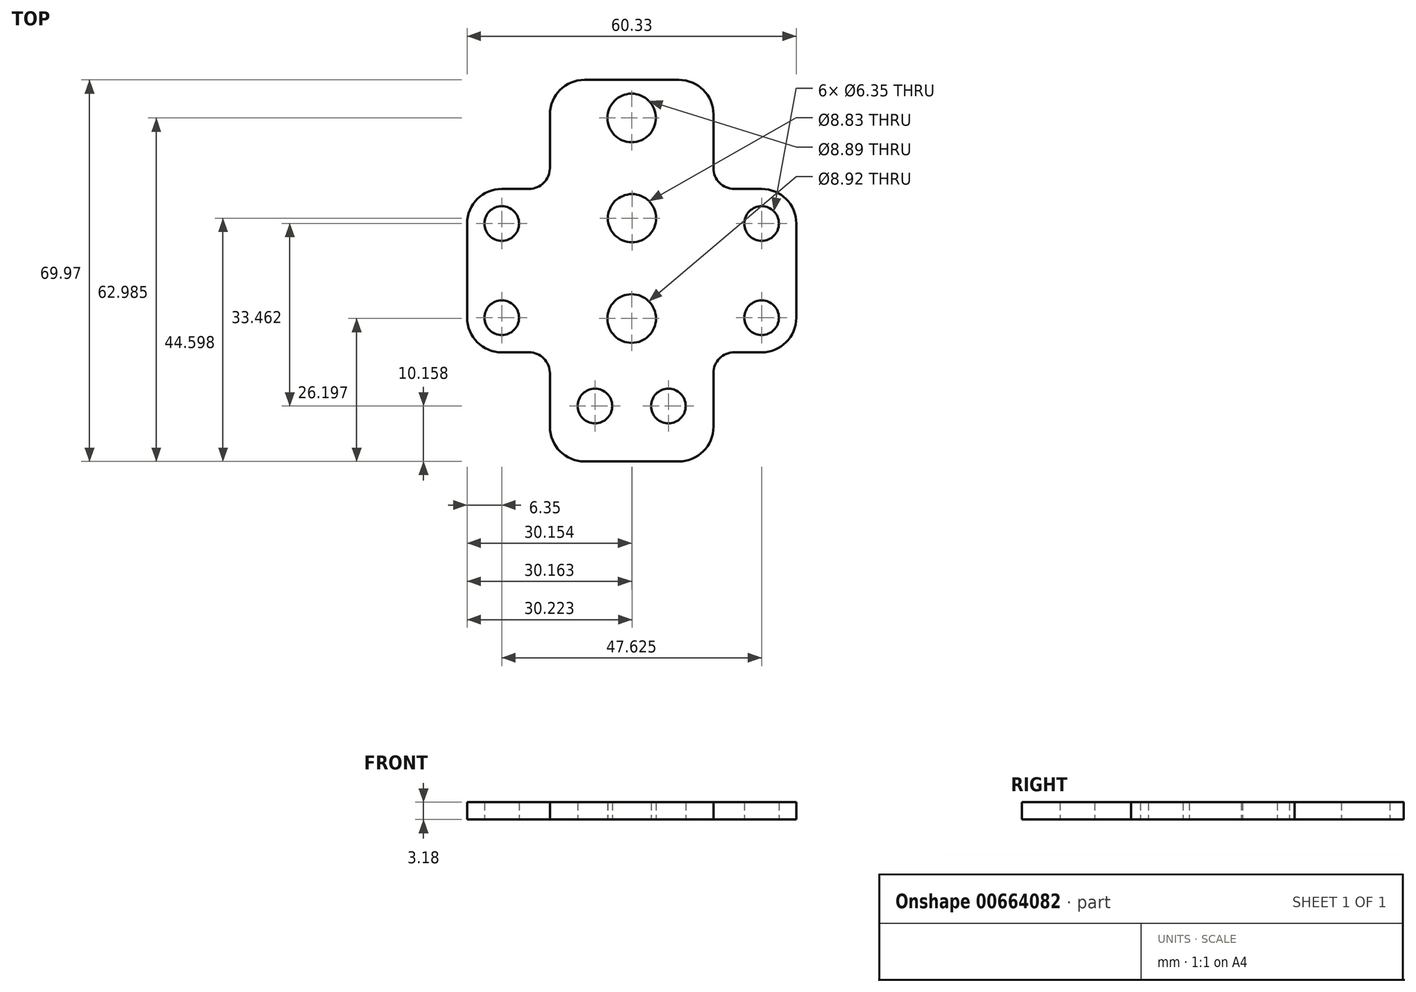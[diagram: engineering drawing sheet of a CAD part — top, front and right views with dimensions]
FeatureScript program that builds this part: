
annotation { "Feature Type Name" : "Feature", "Feature Type Description" : "" }
export const myFeature = defineFeature(function(context is Context, id is Id, definition is map)
    precondition{}
    {
        {
            var Q0;
            Q0=qCreatedBy(makeId("Top.planeOp"),FACE);
            var sketch = newSketch(context, id + "F0", { "sketchPlane" : qUnion([Q0])});
            skLineSegment(sketch, "E0.bottom", {"start": v(6.35, 0) * mm, "end": v(11.36, 0) * mm});
            skLineSegment(sketch, "E0.top", {"start": v(6.35, -29.97) * mm, "end": v(11.36, -29.97) * mm});
            skLineSegment(sketch, "E0.left", {"start": v(0, -6.35) * mm, "end": v(0, -23.62) * mm});
            skLineSegment(sketch, "E0.right", {"start": v(60.32, -6.35) * mm, "end": v(60.32, -23.62) * mm});
            skLineSegment(sketch, "E1.top", {"start": v(21.52, -49.97) * mm, "end": v(38.8, -49.97) * mm});
            skLineSegment(sketch, "E1.left", {"start": v(15.17, -33.78) * mm, "end": v(15.17, -43.62) * mm});
            skLineSegment(sketch, "E1.right", {"start": v(45.15, -33.78) * mm, "end": v(45.15, -43.62) * mm});
            skLineSegment(sketch, "E2.top", {"start": v(21.52, 20) * mm, "end": v(38.8, 20) * mm});
            skLineSegment(sketch, "E2.left", {"start": v(15.17, 3.81) * mm, "end": v(15.17, 13.65) * mm});
            skLineSegment(sketch, "E2.right", {"start": v(45.15, 3.8) * mm, "end": v(45.15, 13.65) * mm});
            skLineSegment(sketch, "E3.trimOffspring", {"start": v(48.96, 0) * mm, "end": v(53.97, 0) * mm});
            skLineSegment(sketch, "E4.trimOffspring", {"start": v(48.96, -29.97) * mm, "end": v(53.97, -29.97) * mm});
            skPoint(sketch, "E5.visualSharp", {"position": v(15.17, 20) * mm});
            skArc(sketch, "E5.filletArc", {"start": v(21.52, 20) * mm, "mid": v(17.03, 18.14) * mm, "end": v(15.17, 13.65) * mm});
            skPoint(sketch, "E6.visualSharp", {"position": v(45.15, 20) * mm});
            skArc(sketch, "E6.filletArc", {"start": v(45.15, 13.65) * mm, "mid": v(43.29, 18.14) * mm, "end": v(38.8, 20) * mm});
            skPoint(sketch, "E7.visualSharp", {"position": v(15.17, -49.97) * mm});
            skArc(sketch, "E7.filletArc", {"start": v(15.17, -43.62) * mm, "mid": v(17.03, -48.11) * mm, "end": v(21.52, -49.97) * mm});
            skPoint(sketch, "E8.visualSharp", {"position": v(45.15, -49.97) * mm});
            skArc(sketch, "E8.filletArc", {"start": v(38.8, -49.97) * mm, "mid": v(43.29, -48.11) * mm, "end": v(45.15, -43.62) * mm});
            skPoint(sketch, "E9.visualSharp", {"position": v(60.33, -29.97) * mm});
            skArc(sketch, "E9.filletArc", {"start": v(53.97, -29.97) * mm, "mid": v(58.47, -28.11) * mm, "end": v(60.32, -23.62) * mm});
            skPoint(sketch, "E10.visualSharp", {"position": v(60.32, 0) * mm});
            skArc(sketch, "E10.filletArc", {"start": v(60.32, -6.35) * mm, "mid": v(58.47, -1.86) * mm, "end": v(53.97, 0) * mm});
            skPoint(sketch, "E11.visualSharp", {"position": v(0, 0) * mm});
            skArc(sketch, "E11.filletArc", {"start": v(6.35, 0) * mm, "mid": v(1.86, -1.86) * mm, "end": v(0, -6.35) * mm});
            skPoint(sketch, "E12.visualSharp", {"position": v(0, -29.97) * mm});
            skArc(sketch, "E12.filletArc", {"start": v(0, -23.62) * mm, "mid": v(1.86, -28.11) * mm, "end": v(6.35, -29.97) * mm});
            skPoint(sketch, "E13.visualSharp", {"position": v(45.15, 0) * mm});
            skArc(sketch, "E13.filletArc", {"start": v(45.15, 3.8) * mm, "mid": v(46.26, 1.12) * mm, "end": v(48.96, 0) * mm});
            skPoint(sketch, "E14.visualSharp", {"position": v(15.17, 0) * mm});
            skArc(sketch, "E14.filletArc", {"start": v(11.36, 0) * mm, "mid": v(14.06, 1.12) * mm, "end": v(15.17, 3.81) * mm});
            skPoint(sketch, "E15.visualSharp", {"position": v(15.17, -29.97) * mm});
            skArc(sketch, "E15.filletArc", {"start": v(15.17, -33.78) * mm, "mid": v(14.06, -31.09) * mm, "end": v(11.36, -29.97) * mm});
            skPoint(sketch, "E16.visualSharp", {"position": v(45.15, -29.97) * mm});
            skArc(sketch, "E16.filletArc", {"start": v(48.96, -29.97) * mm, "mid": v(46.26, -31.09) * mm, "end": v(45.15, -33.78) * mm});
            skCircle(sketch, "E17", {"center": v(23.43, -39.81) * mm, "radius": 3.18 * mm});
            skCircle(sketch, "E18", {"center": v(36.9, -39.81) * mm, "radius": 3.18 * mm});
            skCircle(sketch, "E19", {"center": v(6.35, -6.35) * mm, "radius": 3.18 * mm});
            skCircle(sketch, "E20", {"center": v(6.35, -23.62) * mm, "radius": 3.18 * mm});
            skCircle(sketch, "E21", {"center": v(53.97, -6.35) * mm, "radius": 3.18 * mm});
            skCircle(sketch, "E22", {"center": v(53.97, -23.62) * mm, "radius": 3.18 * mm});
            skCircle(sketch, "E23", {"center": v(30.15, 13.01) * mm, "radius": 4.45 * mm});
            skCircle(sketch, "E24", {"center": v(30.22, -5.37) * mm, "radius": 4.42 * mm});
            skCircle(sketch, "E25", {"center": v(30.16, -23.77) * mm, "radius": 4.46 * mm});
            skSolve(sketch);
        }
        {
            var Q0;
            Q0=makeQuery(id+"F0.imprint","IMPRINT",FACE,{"disambiguationData":[TD([[makeQuery(id+"F0.imprint","IMPRINT",EDGE,{"derivedFrom":sQuery(id+"F0.wireOp",EDGE,"E0.bottom")}),-1.0]])]});
            extrude(context, id + "F1", {"entities" : qUnion([Q0]), "depth" : 3.17 * mm, "offsetDistance" : 25.4 * mm});
        }
    });
